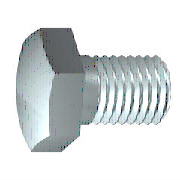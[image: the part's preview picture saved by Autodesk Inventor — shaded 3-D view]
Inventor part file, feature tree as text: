
AUTODESK INVENTOR PART (.ipt)
format: ipt  version: 2023 (Build 270158000, 158)  size: 188,928 bytes
history: native  units: mm (DEFAULTED — no unit token found)
features: other x2, sketch x2, extrude x1, fillet x1, plane x1
ambient origin geometry x7: Origin, YZ Plane, XZ Plane, X Axis, Y Axis, Z Axis, Center Point
bodies: Solid1 (feature_tree)
feature tree (7):
  other  "Базовый элемент"
  extrude  "С головкой"  Depth=10.0mm
  other  "Фаска1"
  fillet  "Fillet"  [1 undecoded]
  plane  "Work Plane1"
  sketch  "Эскиз1"
  sketch  "Эскиз2"
note: 1 required parameter value undecoded (feature->parameter linkage not recoverable at this tier; creation-order binding heuristic only, values carry confidence <= 0.55)
